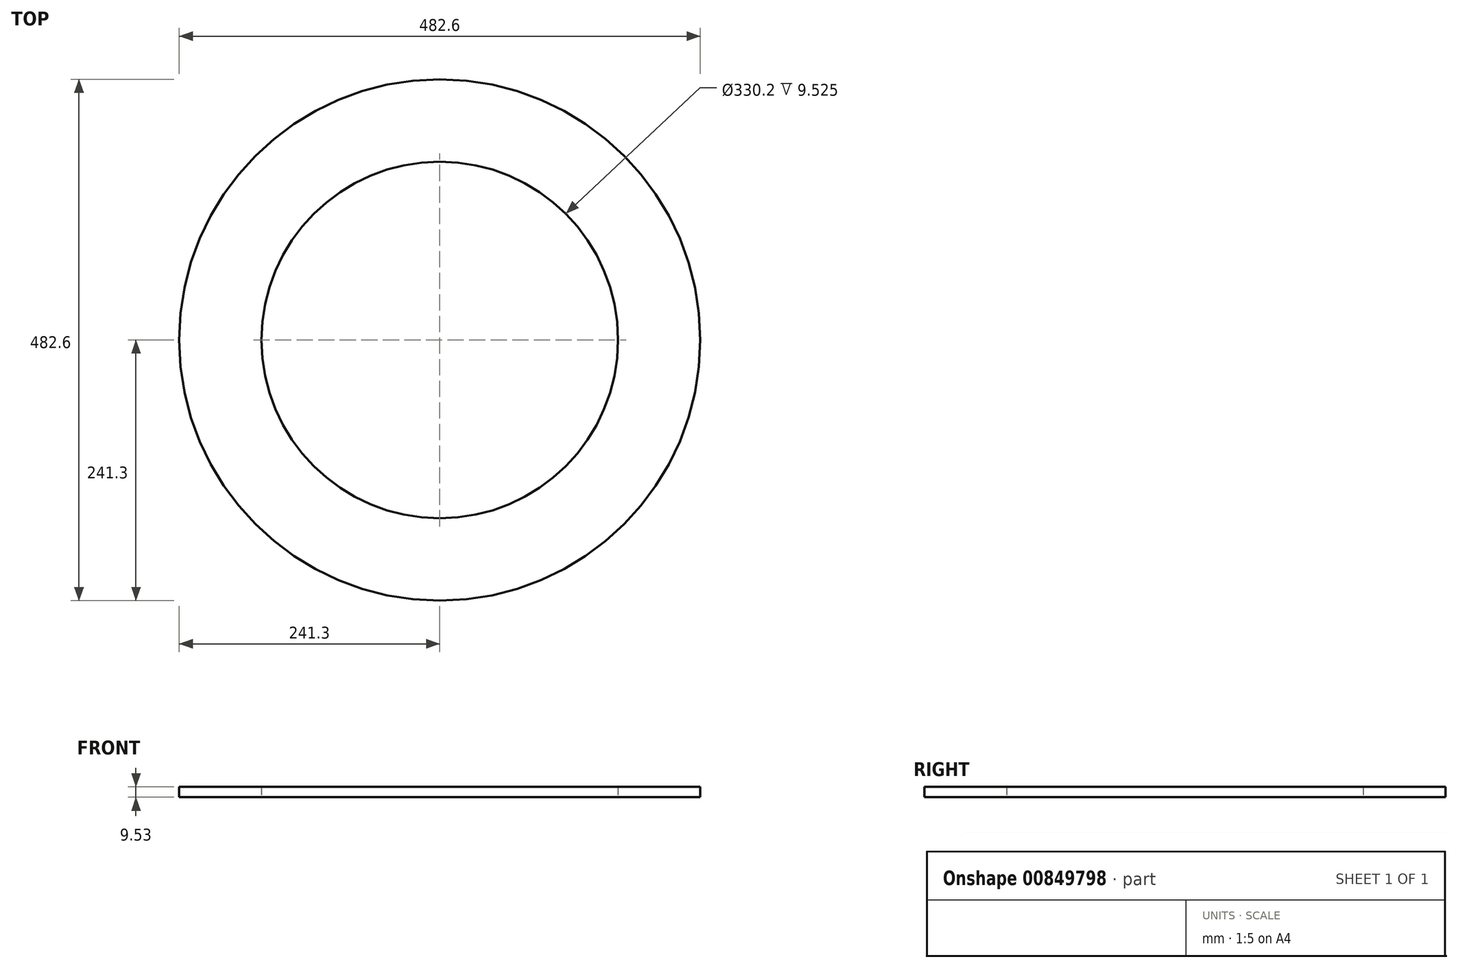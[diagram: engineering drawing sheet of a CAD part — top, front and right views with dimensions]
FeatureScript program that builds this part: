
annotation { "Feature Type Name" : "Feature", "Feature Type Description" : "" }
export const myFeature = defineFeature(function(context is Context, id is Id, definition is map)
    precondition{}
    {
        {
            var Q0;
            Q0=qCreatedBy(makeId("Top.planeOp"),FACE);
            var sketch = newSketch(context, id + "F0", { "sketchPlane" : qUnion([Q0])});
            skCircle(sketch, "E0", {"center": v(0, 0) * mm, "radius": 241.3 * mm});
            skCircle(sketch, "E1", {"center": v(0, 0) * mm, "radius": 165.1 * mm});
            skSolve(sketch);
        }
        {
            var Q0;
            Q0 = qSketchRegion(id + "F0", true);
            extrude(context, id + "F1", {"entities" : qUnion([Q0]), "depth" : 9.52 * mm, "offsetDistance" : 25 * mm});
        }
    });
